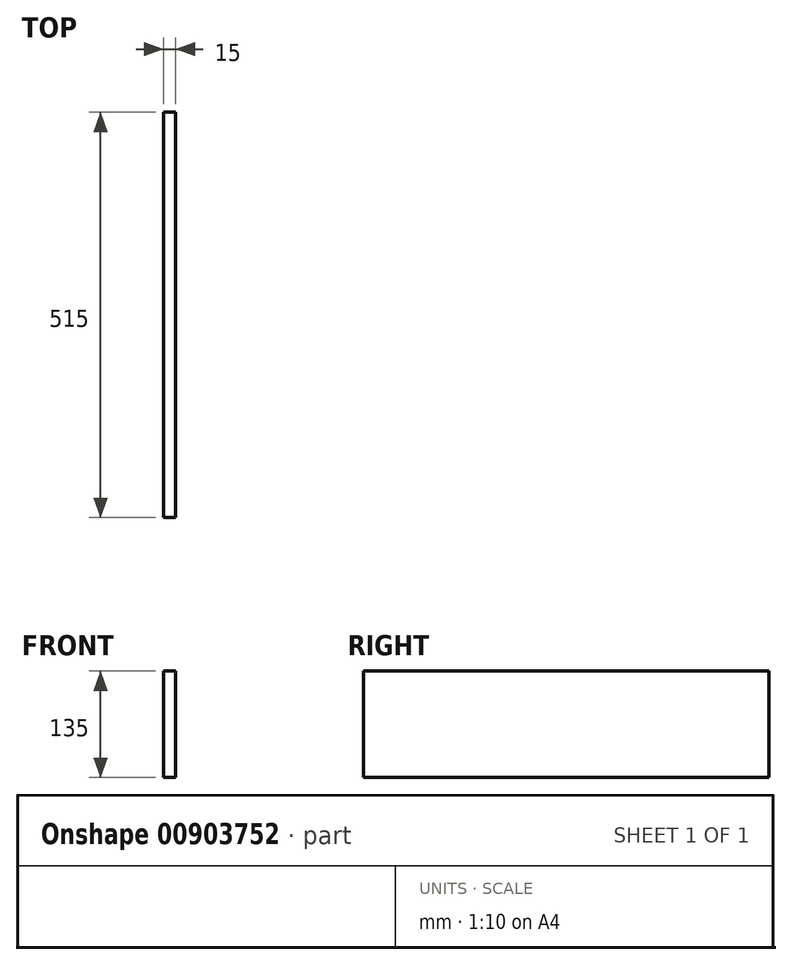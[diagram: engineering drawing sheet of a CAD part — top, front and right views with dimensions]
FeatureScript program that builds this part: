
annotation { "Feature Type Name" : "Feature", "Feature Type Description" : "" }
export const myFeature = defineFeature(function(context is Context, id is Id, definition is map)
    precondition{}
    {
        {
            var Q0;
            Q0=qCreatedBy(makeId("Right.planeOp"),FACE);
            var sketch = newSketch(context, id + "F0", { "sketchPlane" : qUnion([Q0])});
            skLineSegment(sketch, "E0.bottom", {"start": v(-257.5, 67.5) * mm, "end": v(257.5, 67.5) * mm});
            skLineSegment(sketch, "E0.top", {"start": v(-257.5, -67.5) * mm, "end": v(257.5, -67.5) * mm});
            skLineSegment(sketch, "E0.left", {"start": v(-257.5, 67.5) * mm, "end": v(-257.5, -67.5) * mm});
            skLineSegment(sketch, "E0.right", {"start": v(257.5, 67.5) * mm, "end": v(257.5, -67.5) * mm});
            skSolve(sketch);
        }
        {
            var Q0;
            Q0=makeQuery(id+"F0.imprint","IMPRINT",FACE,{"disambiguationData":[TD([[makeQuery(id+"F0.imprint","IMPRINT",EDGE,{"derivedFrom":sQuery(id+"F0.wireOp",EDGE,"E0.bottom")}),-1.0]])]});
            extrude(context, id + "F1", {"entities" : qUnion([Q0]), "depth" : 15 * mm, "offsetDistance" : 25 * mm});
        }
    });
